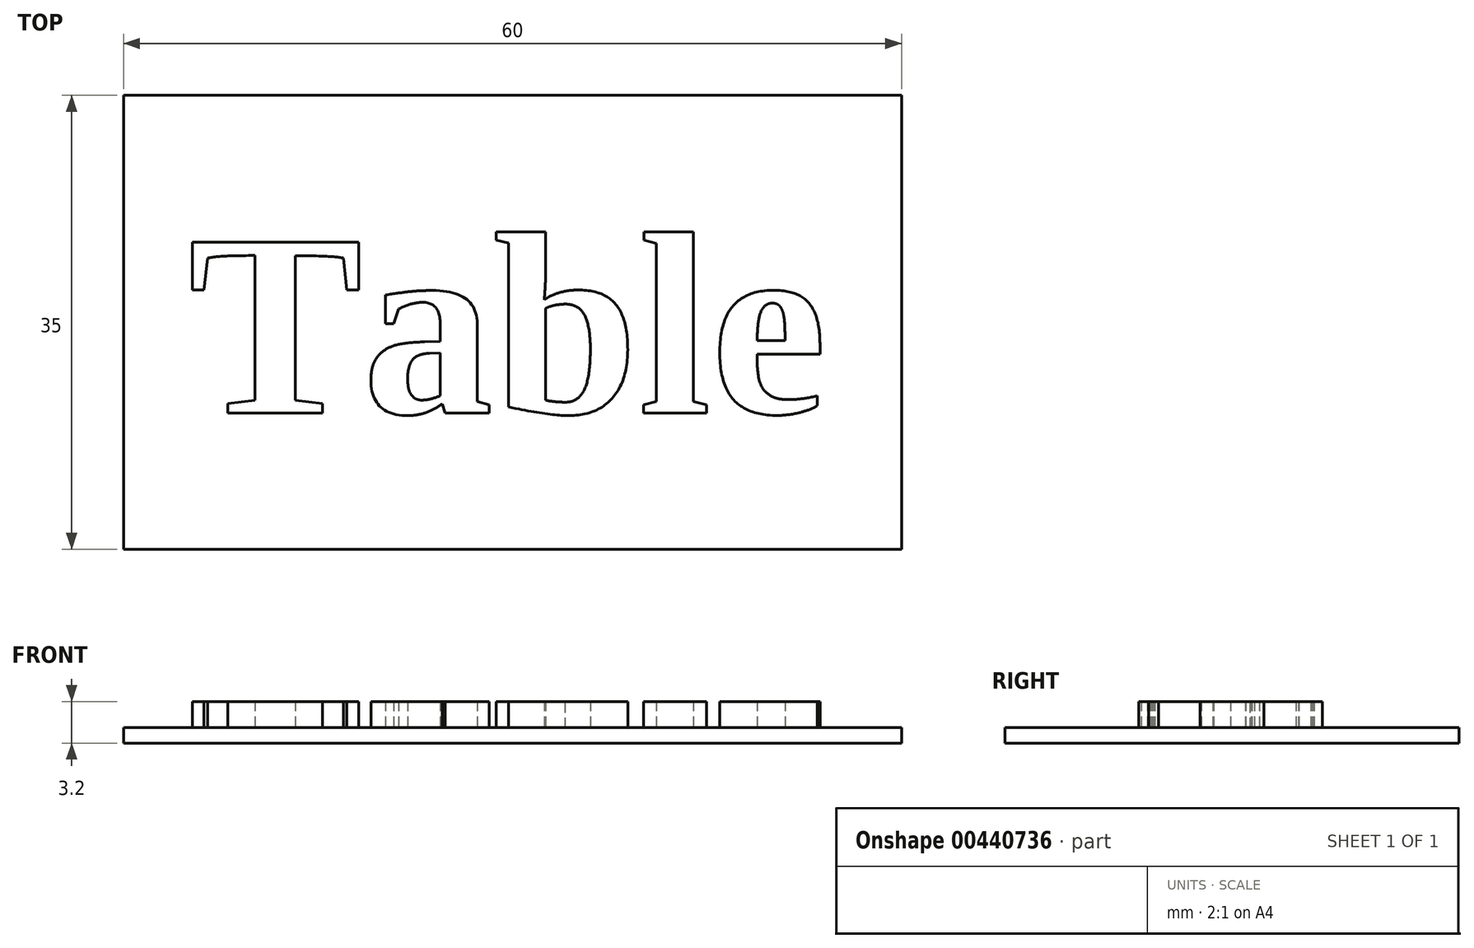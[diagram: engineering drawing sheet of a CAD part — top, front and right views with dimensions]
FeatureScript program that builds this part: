
annotation { "Feature Type Name" : "Feature", "Feature Type Description" : "" }
export const myFeature = defineFeature(function(context is Context, id is Id, definition is map)
    precondition{}
    {
        {
            var Q0;
            Q0=qCreatedBy(makeId("Top.planeOp"),FACE);
            var sketch = newSketch(context, id + "F0", { "sketchPlane" : qUnion([Q0])});
            skLineSegment(sketch, "E0.bottom", {"start": v(0, 0) * mm, "end": v(60, 0) * mm});
            skLineSegment(sketch, "E0.top", {"start": v(0, 35) * mm, "end": v(60, 35) * mm});
            skLineSegment(sketch, "E0.left", {"start": v(0, 0) * mm, "end": v(0, 35) * mm});
            skLineSegment(sketch, "E0.right", {"start": v(60, 0) * mm, "end": v(60, 35) * mm});
            skSolve(sketch);
        }
        {
            var Q0;
            Q0 = qSketchRegion(id + "F0", true);
            extrude(context, id + "F1", {"entities" : qUnion([Q0]), "depth" : 1.2 * mm});
        }
        {
            var Q0;
            Q0=makeQuery(id+"F1.opExtrude","CAP_FACE",FACE,{"disambiguationData":[OSD([sQuery(id+"F0.wireOp",EDGE,"E0.bottom"),sQuery(id+"F0.wireOp",EDGE,"E0.top"),sQuery(id+"F0.wireOp",EDGE,"E0.left"),sQuery(id+"F0.wireOp",EDGE,"E0.right")])],"isStart":false});
            var sketch = newSketch(context, id + "F2", { "sketchPlane" : qUnion([Q0])});
            skText(sketch, "E1", { "text": "Table", "fontName": "Tinos-Bold.ttf"});
            const initialGuessF2  = {"E1": [0.005, 0.0105, 1, 0, 0.0145]};
            skSetInitialGuess(sketch, initialGuessF2);
            skSolve(sketch);
        }
        {
            var Q0;
            Q0 = qSketchRegion(id + "F2", true);
            extrude(context, id + "F3", {"entities" : qUnion([Q0]), "operationType" : NewBodyOperationType.ADD, "depth" : 2 * mm});
        }
    });
